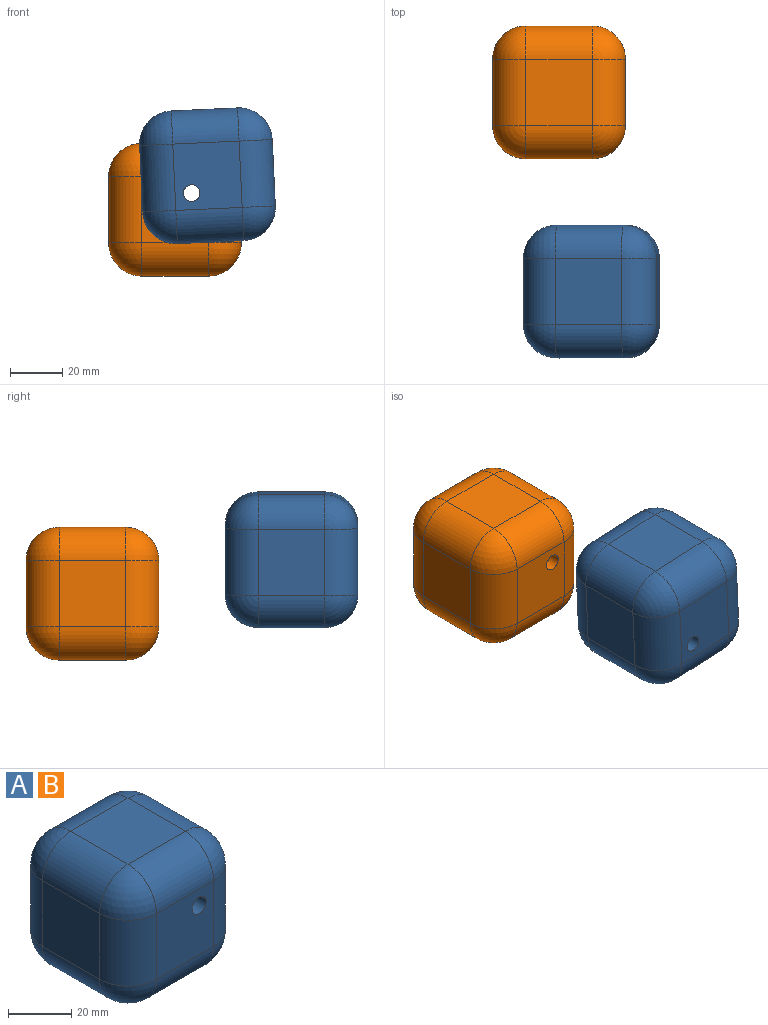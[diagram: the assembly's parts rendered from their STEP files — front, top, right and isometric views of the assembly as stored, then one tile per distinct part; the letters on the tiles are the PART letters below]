
ASSEMBLY  parts=2 mates=1
PART A: 27 faces, bbox 50.8x50.8x50.8 mm
  f0: plane 25.4x25.4mm, normal (-1,0,0), area 645.2mm2, adj f14,f19,f22,f25
  f1: plane 25.4x25.4mm, normal (0,-1,0), area 613.5mm2, adj f11,f20,f21,f25,f26
  f2: plane 25.4x25.4mm, normal (1,0,0), area 645.2mm2, adj f6,f10,f11,f12
  f3: plane 25.4x25.4mm, normal (0,1,0), area 613.5mm2, adj f6,f9,f13,f14,f26
  f4: plane 25.4x25.4mm, normal (0,0,1), area 645.2mm2, adj f9,f10,f19,f20
  f5: plane 25.4x25.4mm, normal (0,0,-1), area 645.2mm2, adj f12,f13,f21,f22
  f6: cylinder r=12.7mm len=25.4mm, axis (0,0,1), area 506.7mm2, adj f2,f3,f7,f8
  f7: sphere r=12.7mm, area 253.4mm2, adj f6,f9,f10
  f8: sphere r=12.7mm, area 253.4mm2, adj f6,f12,f13
  f9: cylinder r=12.7mm len=25.4mm, axis (1,0,0), area 506.7mm2, adj f3,f4,f7,f15
  f10: cylinder r=12.7mm len=25.4mm, axis (0,-1,0), area 506.7mm2, adj f2,f4,f7,f16
  f11: cylinder r=12.7mm len=25.4mm, axis (0,0,-1), area 506.7mm2, adj f1,f2,f16,f17
  f12: cylinder r=12.7mm len=25.4mm, axis (0,1,0), area 506.7mm2, adj f2,f5,f8,f17
  f13: cylinder r=12.7mm len=25.4mm, axis (-1,0,0), area 506.7mm2, adj f3,f5,f8,f18
  f14: cylinder r=12.7mm len=25.4mm, axis (0,0,-1), area 506.7mm2, adj f0,f3,f15,f18
  f15: sphere r=12.7mm, area 253.4mm2, adj f9,f14,f19
  f16: sphere r=12.7mm, area 253.4mm2, adj f10,f11,f20
  f17: sphere r=12.7mm, area 253.4mm2, adj f11,f12,f21
  f18: sphere r=12.7mm, area 253.4mm2, adj f13,f14,f22
  f19: cylinder r=12.7mm len=25.4mm, axis (0,1,0), area 506.7mm2, adj f0,f4,f15,f23
  f20: cylinder r=12.7mm len=25.4mm, axis (-1,0,0), area 506.7mm2, adj f1,f4,f16,f23
  f21: cylinder r=12.7mm len=25.4mm, axis (1,0,0), area 506.7mm2, adj f1,f5,f17,f24
  f22: cylinder r=12.7mm len=25.4mm, axis (0,-1,0), area 506.7mm2, adj f0,f5,f18,f24
  f23: sphere r=12.7mm, area 253.4mm2, adj f19,f20,f25
  f24: sphere r=12.7mm, area 253.4mm2, adj f21,f22,f25
  f25: cylinder r=12.7mm len=25.4mm, axis (0,0,1), area 506.7mm2, adj f0,f1,f23,f24
  f26: cylinder r=3.17mm len=50.8mm, axis (0,-1,0), area 1013.4mm2, adj f1,f3
PART B: same geometry as A
PLACE A rot(axis=(0.72,0,-0.69),180deg) t=(-4.32,-50.4,75.57)mm
PLACE B t=(-66.33,-25,10.65)mm fixed
MATE revolute A.f26 <-> B.f26  axis (0,1,0) through (-34.58,-50.4,42.4)mm
